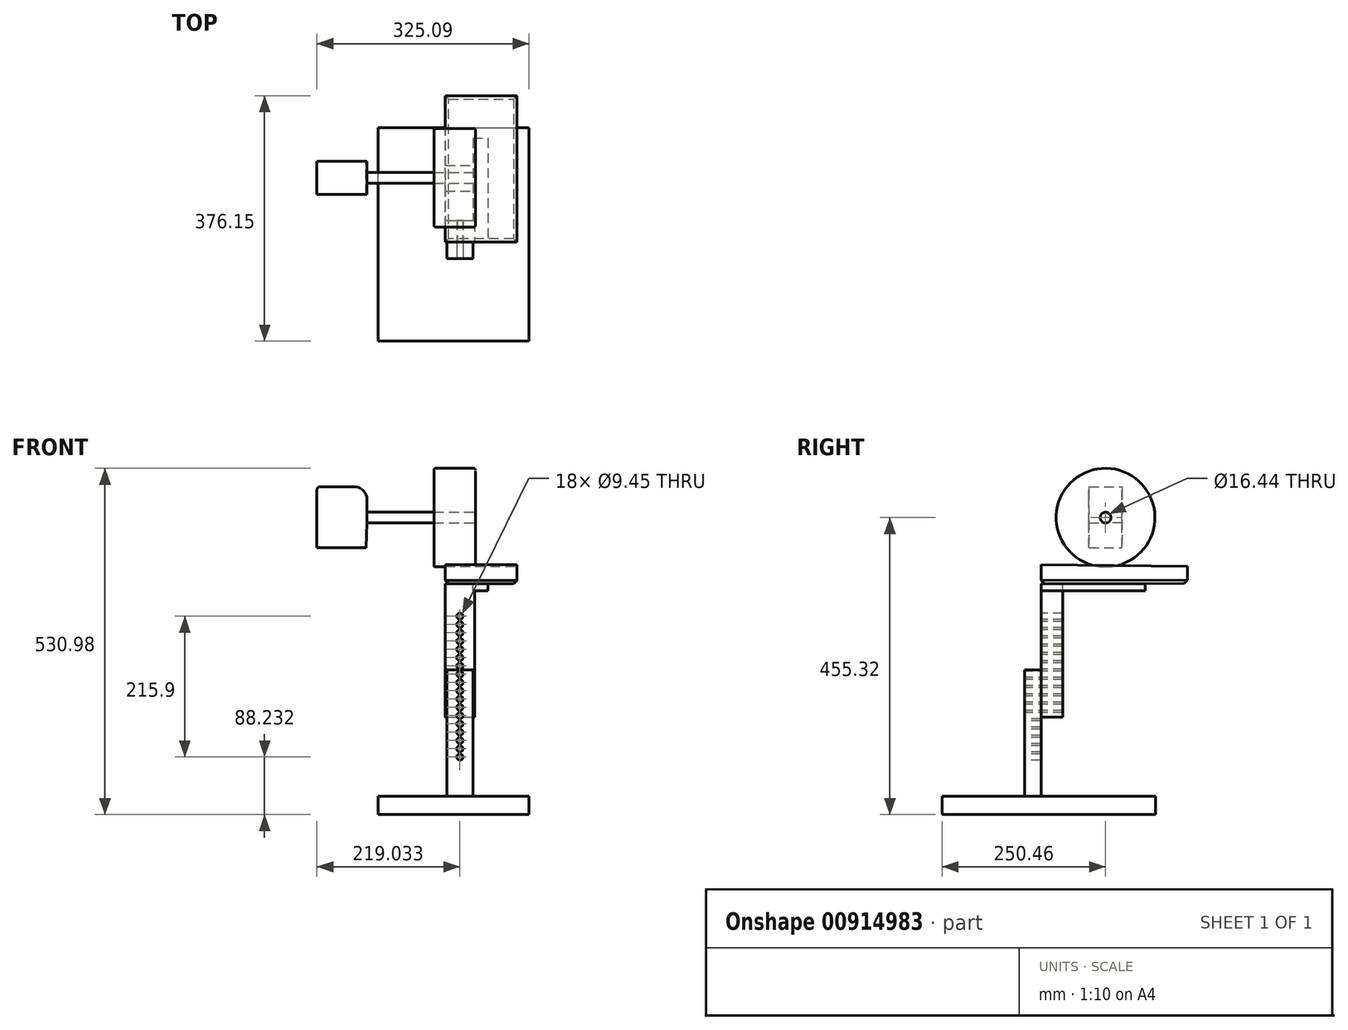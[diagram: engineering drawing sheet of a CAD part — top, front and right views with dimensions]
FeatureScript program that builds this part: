
annotation { "Feature Type Name" : "Feature", "Feature Type Description" : "" }
export const myFeature = defineFeature(function(context is Context, id is Id, definition is map)
    precondition{}
    {
        {
            var Q0;
            Q0=qCreatedBy(makeId("Right.planeOp"),FACE);
            var sketch = newSketch(context, id + "F0", { "sketchPlane" : qUnion([Q0])});
            skCircle(sketch, "E0", {"center": v(0, 0) * mm, "radius": 75.66 * mm});
            skSolve(sketch);
        }
        {
            var Q0;
            Q0=makeQuery(id+"F0.imprint","IMPRINT",FACE,{"disambiguationData":[TD([[makeQuery(id+"F0.imprint","IMPRINT",EDGE,{"derivedFrom":sQuery(id+"F0.wireOp",EDGE,"E0")}),1.0]])]});
            var Q1;
            Q1=sQuery(id+"F0.wireOp",EDGE,"E0");
            extrude(context, id + "F1", {"entities" : qUnion([Q0]), "surfaceEntities" : qUnion([Q1]), "oppositeDirection" : true, "depth" : 63.5 * mm, "offsetDistance" : 25.4 * mm});
        }
        {
            var Q0;
            Q0=makeQuery(id+"F1.opExtrude","CAP_FACE",FACE,{"disambiguationData":[OSD([sQuery(id+"F0.wireOp",EDGE,"E0")])],"isStart":true});
            var sketch = newSketch(context, id + "F2", { "sketchPlane" : qUnion([Q0])});
            skCircle(sketch, "E1", {"center": v(0, 0) * mm, "radius": 8.22 * mm});
            skSolve(sketch);
        }
        {
            var Q0;
            Q0=makeQuery(id+"F2.imprint","IMPRINT",FACE,{"disambiguationData":[TD([[makeQuery(id+"F2.imprint","IMPRINT",EDGE,{"derivedFrom":sQuery(id+"F2.wireOp",EDGE,"E1")}),1.0]])]});
            extrude(context, id + "F3", {"entities" : qUnion([Q0]), "operationType" : NewBodyOperationType.REMOVE, "oppositeDirection" : true, "depth" : 76.2 * mm, "offsetDistance" : 25.4 * mm});
        }
        {
            var Q0;
            Q0=makeQuery(id+"F1.opExtrude","CAP_FACE",FACE,{"disambiguationData":[OSD([sQuery(id+"F0.wireOp",EDGE,"E0")])],"isStart":false});
            var sketch = newSketch(context, id + "F4", { "sketchPlane" : qUnion([Q0])});
            skCircle(sketch, "E2", {"center": v(0, 0) * mm, "radius": 8.2 * mm});
            skSolve(sketch);
        }
        {
            var Q0;
            Q0 = qSketchRegion(id + "F4", true);
            extrude(context, id + "F5", {"entities" : qUnion([Q0]), "depth" : 102.62 * mm, "offsetDistance" : 25.4 * mm});
        }
        {
            var Q0;
            Q0=makeQuery(id+"F1.opExtrude","CAP_EDGE",EDGE,{"disambiguationData":[OSD([sQuery(id+"F0.wireOp",EDGE,"E0")])],"isStart":false});
            fillet(context, id + "F6", {"entities" : qUnion([Q0]), "radius" : 2.54 * mm, "tangentPropagation" : true, "allowEdgeOverflow" : false});
        }
        {
            var Q0;
            Q0=makeQuery(id+"F1.opExtrude","CAP_EDGE",EDGE,{"disambiguationData":[OSD([sQuery(id+"F0.wireOp",EDGE,"E0")])],"isStart":true});
            fillet(context, id + "F7", {"entities" : qUnion([Q0]), "radius" : 2.54 * mm, "tangentPropagation" : true, "allowEdgeOverflow" : false});
        }
        {
            var Q0;
            Q0=qCreatedBy(makeId("Front.planeOp"),FACE);
            var sketch = newSketch(context, id + "F8", { "sketchPlane" : qUnion([Q0])});
            skLineSegment(sketch, "E3", {"start": v(-166.1, -8) * mm, "end": v(-166.1, 47.52) * mm});
            skLineSegment(sketch, "E4", {"start": v(-166.1, 47.52) * mm, "end": v(-242.77, 47.52) * mm});
            skLineSegment(sketch, "E5", {"start": v(-242.77, 47.52) * mm, "end": v(-242.77, -46.21) * mm});
            skLineSegment(sketch, "E6", {"start": v(-242.77, -46.21) * mm, "end": v(-167.66, -46.21) * mm});
            skLineSegment(sketch, "E7", {"start": v(-167.66, -46.21) * mm, "end": v(-166.1, -8) * mm});
            skSolve(sketch);
        }
        {
            var Q0;
            Q0 = qSketchRegion(id + "F8", true);
            extrude(context, id + "F9", {"entities" : qUnion([Q0]), "operationType" : NewBodyOperationType.ADD, "depth" : 25.4 * mm, "offsetDistance" : 25.4 * mm});
        }
        {
            var Q0;
            Q0=makeQuery(id+"F9.opExtrude","CAP_FACE",FACE,{"disambiguationData":[OSD([sQuery(id+"F8.wireOp",EDGE,"E3"),sQuery(id+"F8.wireOp",EDGE,"E4"),sQuery(id+"F8.wireOp",EDGE,"E5"),sQuery(id+"F8.wireOp",EDGE,"E6"),sQuery(id+"F8.wireOp",EDGE,"E7")])],"isStart":true});
            extrude(context, id + "F10", {"entities" : qUnion([Q0]), "operationType" : NewBodyOperationType.ADD, "depth" : 25.4 * mm, "offsetDistance" : 25.4 * mm});
        }
        {
            var Q0;
            Q0=makeQuery(id+"F1.opExtrude","CAP_FACE",FACE,{"disambiguationData":[OSD([sQuery(id+"F0.wireOp",EDGE,"E0")])],"isStart":true});
            var sketch = newSketch(context, id + "F11", { "sketchPlane" : qUnion([Q0])});
            skLineSegment(sketch, "E8", {"start": v(-98.94, -101.69) * mm, "end": v(-98.94, -71.99) * mm});
            skLineSegment(sketch, "E9", {"start": v(-98.94, -71.99) * mm, "end": v(125.69, -74.56) * mm});
            skLineSegment(sketch, "E10", {"start": v(125.69, -74.56) * mm, "end": v(125.69, -101.03) * mm});
            skLineSegment(sketch, "E11", {"start": v(125.69, -101.03) * mm, "end": v(-98.94, -101.69) * mm});
            skSolve(sketch);
        }
        {
            var Q0;
            Q0 = qSketchRegion(id + "F11", true);
            extrude(context, id + "F12", {"entities" : qUnion([Q0]), "operationType" : NewBodyOperationType.ADD, "oppositeDirection" : true, "depth" : 46.23 * mm, "offsetDistance" : 25.4 * mm, "hasSecondDirection" : true, "secondDirectionOppositeDirection" : false, "secondDirectionDepth" : 63.75 * mm});
        }
        {
            var Q0;
            Q0=makeQuery(id+"F12.opExtrude","SWEPT_FACE",FACE,{"disambiguationData":[OSD([sQuery(id+"F11.wireOp",EDGE,"E8")])]});
            var sketch = newSketch(context, id + "F13", { "sketchPlane" : qUnion([Q0])});
            skLineSegment(sketch, "E12", {"start": v(-46.23, -101.69) * mm, "end": v(-46.23, -305.82) * mm});
            skLineSegment(sketch, "E13", {"start": v(-46.23, -305.82) * mm, "end": v(-1.25, -305.82) * mm});
            skLineSegment(sketch, "E14", {"start": v(-1.25, -305.82) * mm, "end": v(-1.25, -101.69) * mm});
            skLineSegment(sketch, "E15", {"start": v(-1.25, -101.69) * mm, "end": v(-46.23, -101.69) * mm});
            skSolve(sketch);
        }
        {
            var Q0;
            Q0 = qSketchRegion(id + "F13", true);
            extrude(context, id + "F14", {"entities" : qUnion([Q0]), "oppositeDirection" : true, "depth" : 33.53 * mm, "offsetDistance" : 25.4 * mm});
        }
        {
            var Q0;
            Q0=makeQuery(id+"F14.opExtrude","CAP_EDGE",EDGE,{"disambiguationData":[OSD([sQuery(id+"F13.wireOp",EDGE,"E14")])],"isStart":true});
            var Q1;
            Q1=makeQuery(id+"F14.opExtrude","CAP_EDGE",EDGE,{"disambiguationData":[OSD([sQuery(id+"F13.wireOp",EDGE,"E12")])],"isStart":true});
            var Q2;
            Q2=makeQuery(id+"F14.opExtrude","CAP_EDGE",EDGE,{"disambiguationData":[OSD([sQuery(id+"F13.wireOp",EDGE,"E12")])],"isStart":false});
            var Q3;
            Q3=makeQuery(id+"F14.opExtrude","CAP_EDGE",EDGE,{"disambiguationData":[OSD([sQuery(id+"F13.wireOp",EDGE,"E14")])],"isStart":false});
            fillet(context, id + "F15", {"entities" : qUnion([Q0, Q1, Q2, Q3]), "radius" : 2.54 * mm, "tangentPropagation" : true, "allowEdgeOverflow" : false});
        }
        {
            var Q0;
            Q0=makeQuery(id+"F14.opExtrude","CAP_FACE",FACE,{"disambiguationData":[OSD([sQuery(id+"F13.wireOp",EDGE,"E12"),sQuery(id+"F13.wireOp",EDGE,"E13"),sQuery(id+"F13.wireOp",EDGE,"E14"),sQuery(id+"F13.wireOp",EDGE,"E15")])],"isStart":true});
            var sketch = newSketch(context, id + "F16", { "sketchPlane" : qUnion([Q0])});
            skLineSegment(sketch, "E16", {"start": v(-43.69, -238.42) * mm, "end": v(-43.69, -438.46) * mm});
            skLineSegment(sketch, "E17", {"start": v(-43.69, -438.46) * mm, "end": v(-3.79, -438.46) * mm});
            skLineSegment(sketch, "E18", {"start": v(-3.79, -438.46) * mm, "end": v(-3.79, -233.45) * mm});
            skLineSegment(sketch, "E19", {"start": v(-3.79, -233.45) * mm, "end": v(-43.69, -233.45) * mm});
            skLineSegment(sketch, "E20", {"start": v(-43.69, -233.45) * mm, "end": v(-43.69, -238.42) * mm});
            skSolve(sketch);
        }
        {
            var Q0;
            Q0 = qSketchRegion(id + "F16", true);
            extrude(context, id + "F17", {"entities" : qUnion([Q0]), "operationType" : NewBodyOperationType.ADD, "depth" : 25.4 * mm, "offsetDistance" : 25.4 * mm});
        }
        {
            var Q0;
            Q0=makeQuery(id+"F17.opExtrude","SWEPT_FACE",FACE,{"disambiguationData":[OSD([sQuery(id+"F16.wireOp",EDGE,"E18")])]});
            var sketch = newSketch(context, id + "F18", { "sketchPlane" : qUnion([Q0])});
            skLineSegment(sketch, "E21.bottom", {"start": v(-250.46, -426.93) * mm, "end": v(76.88, -426.93) * mm});
            skLineSegment(sketch, "E21.top", {"start": v(-250.46, -455.32) * mm, "end": v(76.88, -455.32) * mm});
            skLineSegment(sketch, "E21.left", {"start": v(-250.46, -426.93) * mm, "end": v(-250.46, -455.32) * mm});
            skLineSegment(sketch, "E21.right", {"start": v(76.88, -426.93) * mm, "end": v(76.88, -455.32) * mm});
            skSolve(sketch);
        }
        {
            var Q0;
            Q0 = qSketchRegion(id + "F18", true);
            extrude(context, id + "F19", {"entities" : qUnion([Q0]), "operationType" : NewBodyOperationType.ADD, "oppositeDirection" : true, "depth" : 145.54 * mm, "offsetDistance" : 25.4 * mm, "hasSecondDirection" : true, "secondDirectionOppositeDirection" : false, "secondDirectionDepth" : 86.1 * mm});
        }
        {
            var Q0;
            Q0=makeQuery(id+"F17.opExtrude","CAP_FACE",FACE,{"disambiguationData":[OSD([sQuery(id+"F16.wireOp",EDGE,"E16"),sQuery(id+"F16.wireOp",EDGE,"E17"),sQuery(id+"F16.wireOp",EDGE,"E18"),sQuery(id+"F16.wireOp",EDGE,"E19"),sQuery(id+"F16.wireOp",EDGE,"E20")])],"isStart":false});
            var sketch = newSketch(context, id + "F20", { "sketchPlane" : qUnion([Q0])});
            skCircle(sketch, "E22", {"center": v(-23.74, -151.19) * mm, "radius": 4.72 * mm});
            skPoint(sketch, "E22.centerSnap0", {"position": v(-23.74, -233.45) * mm});
            skCircle(sketch, "E23.0.1.0", {"center": v(-23.74, -163.89) * mm, "radius": 4.72 * mm});
            skCircle(sketch, "E23.0.2.0", {"center": v(-23.74, -176.59) * mm, "radius": 4.72 * mm});
            skCircle(sketch, "E23.0.3.0", {"center": v(-23.74, -189.29) * mm, "radius": 4.72 * mm});
            skCircle(sketch, "E23.0.4.0", {"center": v(-23.74, -201.99) * mm, "radius": 4.72 * mm});
            skCircle(sketch, "E23.0.5.0", {"center": v(-23.74, -214.69) * mm, "radius": 4.72 * mm});
            skCircle(sketch, "E23.0.6.0", {"center": v(-23.74, -227.39) * mm, "radius": 4.72 * mm});
            skCircle(sketch, "E23.0.7.0", {"center": v(-23.74, -240.09) * mm, "radius": 4.72 * mm});
            skCircle(sketch, "E23.0.8.0", {"center": v(-23.74, -252.79) * mm, "radius": 4.72 * mm});
            skCircle(sketch, "E23.0.9.0", {"center": v(-23.74, -265.49) * mm, "radius": 4.72 * mm});
            skLineSegment(sketch, "E23.direction1", {"start": v(-23.74, -151.19) * mm, "end": v(1.66, -151.19) * mm, "construction": true});
            skLineSegment(sketch, "E23.direction2", {"start": v(-23.74, -151.19) * mm, "end": v(-23.74, -163.89) * mm, "construction": true});
            skCircle(sketch, "E24.0.0.10", {"center": v(-23.74, -278.19) * mm, "radius": 4.72 * mm});
            skCircle(sketch, "E24.0.0.11", {"center": v(-23.74, -290.89) * mm, "radius": 4.72 * mm});
            skCircle(sketch, "E24.0.0.12", {"center": v(-23.74, -303.59) * mm, "radius": 4.72 * mm});
            skCircle(sketch, "E24.0.0.13", {"center": v(-23.74, -316.29) * mm, "radius": 4.72 * mm});
            skCircle(sketch, "E24.0.0.14", {"center": v(-23.74, -328.99) * mm, "radius": 4.72 * mm});
            skCircle(sketch, "E24.0.0.15", {"center": v(-23.74, -341.69) * mm, "radius": 4.72 * mm});
            skCircle(sketch, "E24.0.0.16", {"center": v(-23.74, -354.39) * mm, "radius": 4.72 * mm});
            skCircle(sketch, "E24.0.0.17", {"center": v(-23.74, -367.09) * mm, "radius": 4.72 * mm});
            skSolve(sketch);
        }
        {
            var Q0;
            Q0 = qSketchRegion(id + "F20", true);
            extrude(context, id + "F21", {"entities" : qUnion([Q0]), "operationType" : NewBodyOperationType.REMOVE, "oppositeDirection" : true, "depth" : 68.83 * mm, "offsetDistance" : 25.4 * mm});
        }
        {
            var Q0;
            {var subQ0=sQuery(id+"F8.wireOp",EDGE,"E4");var subQ1=sQuery(id+"F8.wireOp",EDGE,"E3");Q0=makeQuery(id+"F10.boolean.opBoolean","MERGE",EDGE,{"derivedFrom":[makeQuery(id+"F9.opExtrude","SWEPT_EDGE",EDGE,{"disambiguationData":[OSD([subQ1,subQ0])]}),makeQuery(id+"F10.opExtrude","SWEPT_EDGE",EDGE,{"disambiguationData":[OSD([subQ1,subQ0])]})]});}
            fillet(context, id + "F22", {"entities" : qUnion([Q0]), "radius" : 20.32 * mm, "tangentPropagation" : true, "allowEdgeOverflow" : false});
        }
        {
            var Q0;
            {var subQ0=sQuery(id+"F8.wireOp",EDGE,"E5");var subQ1=sQuery(id+"F8.wireOp",EDGE,"E4");Q0=makeQuery(id+"F10.boolean.opBoolean","MERGE",EDGE,{"derivedFrom":[makeQuery(id+"F9.opExtrude","SWEPT_EDGE",EDGE,{"disambiguationData":[OSD([subQ1,subQ0])]}),makeQuery(id+"F10.opExtrude","SWEPT_EDGE",EDGE,{"disambiguationData":[OSD([subQ1,subQ0])]})]});}
            fillet(context, id + "F23", {"entities" : qUnion([Q0]), "radius" : 5.08 * mm, "tangentPropagation" : true, "allowEdgeOverflow" : false});
        }
        {
            var Q0;
            Q0=makeQuery(id+"F12.opExtrude","CAP_EDGE",EDGE,{"disambiguationData":[OSD([sQuery(id+"F11.wireOp",EDGE,"E11")])],"isStart":true});
            var Q1;
            Q1=makeQuery(id+"F12.opExtrude","SWEPT_EDGE",EDGE,{"disambiguationData":[OSD([sQuery(id+"F11.wireOp",EDGE,"E8"),sQuery(id+"F11.wireOp",EDGE,"E11")])]});
            var Q2;
            Q2=makeQuery(id+"F12.opExtrude","CAP_EDGE",EDGE,{"disambiguationData":[OSD([sQuery(id+"F11.wireOp",EDGE,"E11")])],"isStart":false});
            var Q3;
            Q3=makeQuery(id+"F12.opExtrude","SWEPT_EDGE",EDGE,{"disambiguationData":[OSD([sQuery(id+"F11.wireOp",EDGE,"E10"),sQuery(id+"F11.wireOp",EDGE,"E11")])]});
            chamfer(context, id + "F24", {"entities" : qUnion([Q0, Q1, Q2, Q3]), "width" : 5.08 * mm, "tangentPropagation" : true});
        }
        {
            var Q0;
            Q0=makeQuery(id+"F14.opExtrude","CAP_FACE",FACE,{"disambiguationData":[OSD([sQuery(id+"F13.wireOp",EDGE,"E12"),sQuery(id+"F13.wireOp",EDGE,"E13"),sQuery(id+"F13.wireOp",EDGE,"E14"),sQuery(id+"F13.wireOp",EDGE,"E15")])],"isStart":true});
            var sketch = newSketch(context, id + "F25", { "sketchPlane" : qUnion([Q0])});
            skLineSegment(sketch, "E25", {"start": v(-3.79, -101.69) * mm, "end": v(19.21, -101.69) * mm});
            skLineSegment(sketch, "E26", {"start": v(19.21, -101.69) * mm, "end": v(19.21, -111.99) * mm});
            skLineSegment(sketch, "E27", {"start": v(19.21, -111.99) * mm, "end": v(-3.79, -111.99) * mm});
            skLineSegment(sketch, "E28", {"start": v(-3.79, -111.99) * mm, "end": v(-3.79, -101.69) * mm});
            skSolve(sketch);
        }
        {
            var Q0;
            Q0 = qSketchRegion(id + "F25", true);
            extrude(context, id + "F26", {"entities" : qUnion([Q0]), "operationType" : NewBodyOperationType.ADD, "oppositeDirection" : true, "depth" : 159.5 * mm, "offsetDistance" : 25.4 * mm});
        }
    });
